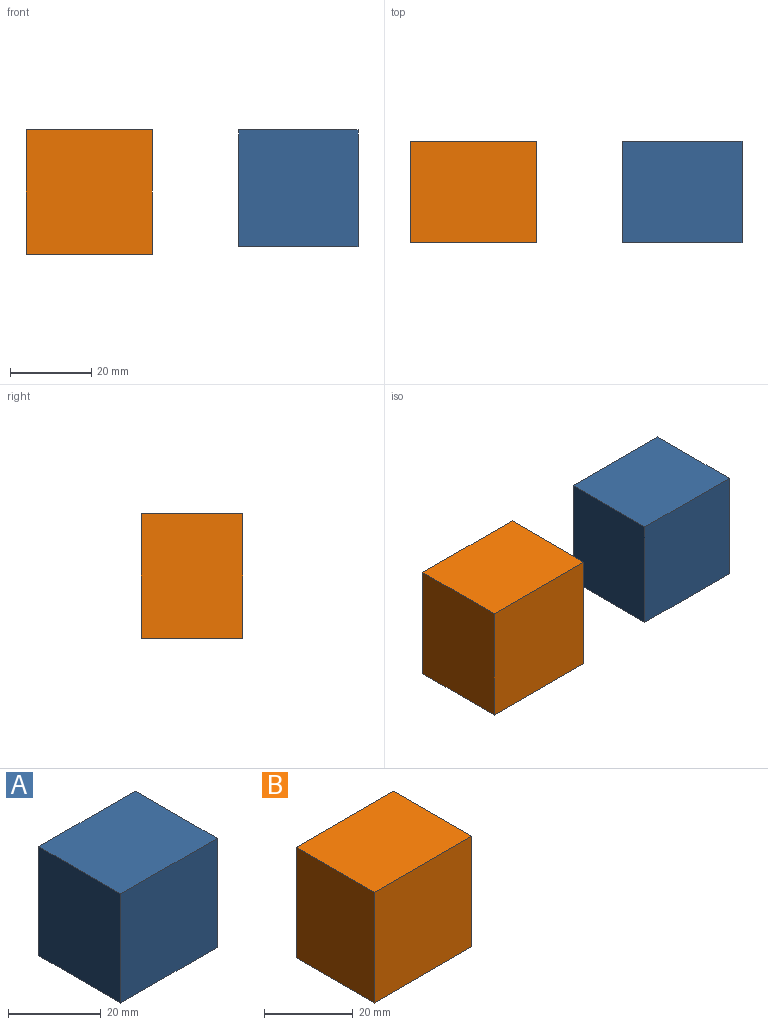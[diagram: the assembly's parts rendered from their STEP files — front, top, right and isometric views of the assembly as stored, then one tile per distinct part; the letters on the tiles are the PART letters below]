
ASSEMBLY  parts=2 mates=1
PART A: 6 faces, bbox 29.4x25x28.8 mm
  f0: plane 29.4x25mm, normal (0,0,1), area 735mm2, adj f1,f3,f4,f5
  f1: plane 28.81x25mm, normal (-1,0,0), area 720.2mm2, adj f0,f2,f4,f5
  f2: plane 29.4x25mm, normal (0,0,-1), area 735mm2, adj f1,f3,f4,f5
  f3: plane 28.81x25mm, normal (1,0,0), area 720.2mm2, adj f0,f2,f4,f5
  f4: plane 29.4x28.81mm, normal (0,-1,0), area 847mm2, adj f0,f1,f2,f3
  f5: plane 29.4x28.81mm, normal (0,1,0), area 847mm2, adj f0,f1,f2,f3
PART B: 6 faces, bbox 31.2x25x30.6 mm
  f0: plane 30.59x25mm, normal (1,0,0), area 764.7mm2, adj f1,f3,f4,f5
  f1: plane 31.18x25mm, normal (0,0,1), area 779.6mm2, adj f0,f2,f4,f5
  f2: plane 30.59x25mm, normal (-1,0,0), area 764.7mm2, adj f1,f3,f4,f5
  f3: plane 31.18x25mm, normal (0,0,-1), area 779.6mm2, adj f0,f2,f4,f5
  f4: plane 31.18x30.59mm, normal (0,-1,0), area 953.9mm2, adj f0,f1,f2,f3
  f5: plane 31.18x30.59mm, normal (0,1,0), area 953.9mm2, adj f0,f1,f2,f3
PLACE A t=(-38.11,0,0)mm
PLACE B at identity fixed
MATE slider B.f0 <-> A.f1  axis (-1,0,0) through (-27.92,-25,0)mm
